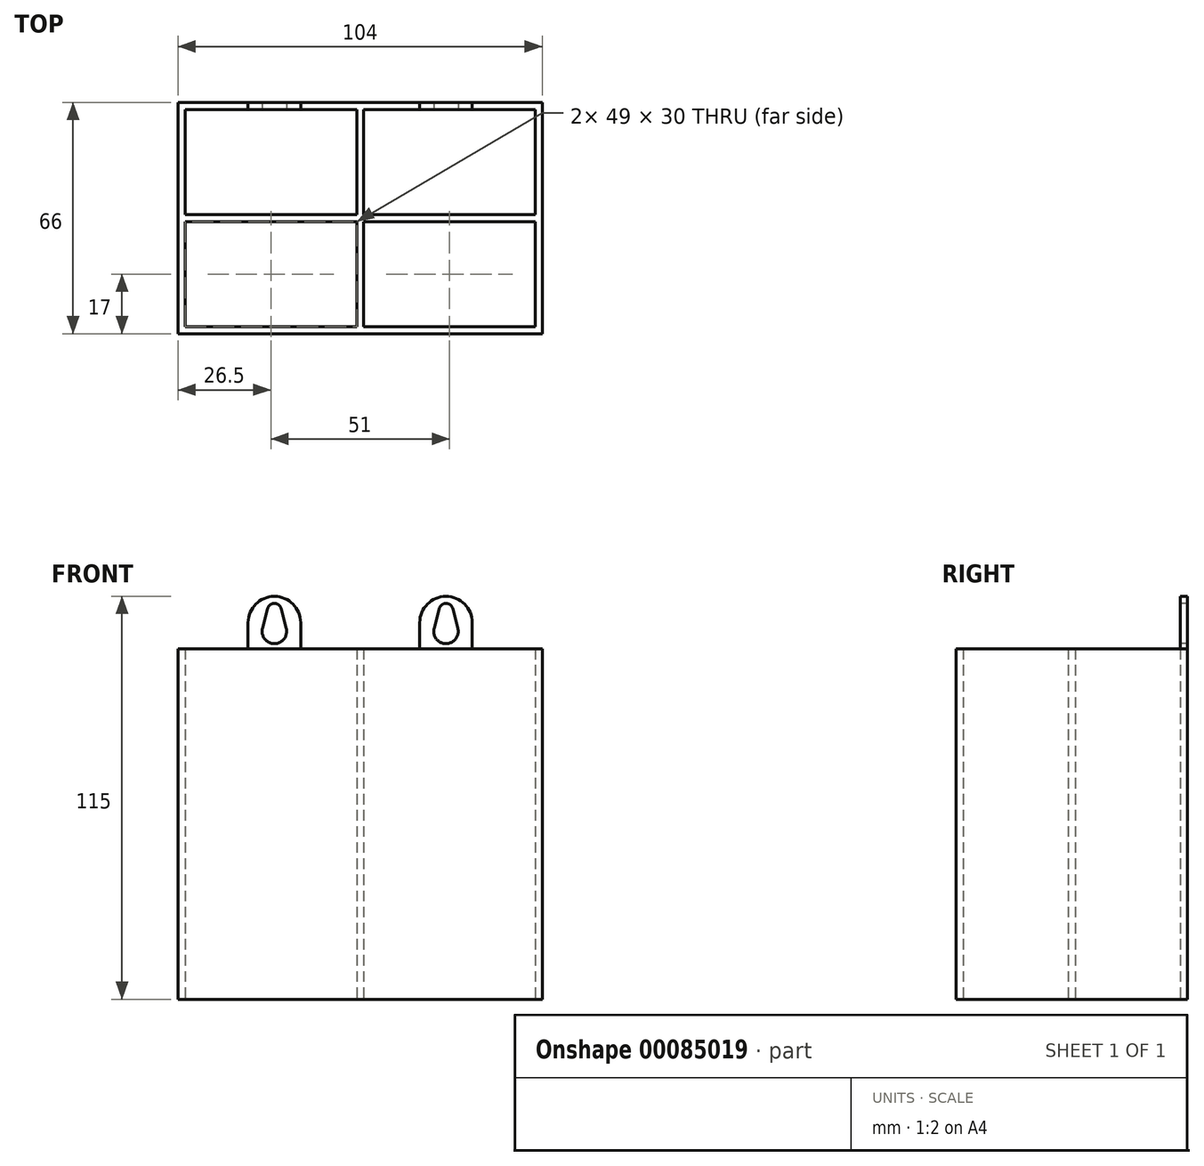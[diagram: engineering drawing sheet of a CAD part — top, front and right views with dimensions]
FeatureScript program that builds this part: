
annotation { "Feature Type Name" : "Feature", "Feature Type Description" : "" }
export const myFeature = defineFeature(function(context is Context, id is Id, definition is map)
    precondition{}
    {
        {
            var Q0;
            Q0=qCreatedBy(makeId("Top.planeOp"),FACE);
            var sketch = newSketch(context, id + "F0", { "sketchPlane" : qUnion([Q0])});
            skLineSegment(sketch, "E0", {"start": v(0, 0) * mm, "end": v(104, 0) * mm});
            skLineSegment(sketch, "E1", {"start": v(0, 0) * mm, "end": v(0, -34) * mm});
            skLineSegment(sketch, "E2", {"start": v(104, 0) * mm, "end": v(104, -34) * mm});
            skLineSegment(sketch, "E3", {"start": v(0, -34) * mm, "end": v(0, -66) * mm});
            skLineSegment(sketch, "E4", {"start": v(0, -66) * mm, "end": v(104, -66) * mm});
            skLineSegment(sketch, "E5", {"start": v(104, -66) * mm, "end": v(104, -34) * mm});
            skSolve(sketch);
        }
        {
            var Q0;
            Q0=qSketchRegion(id+"F0",true);
            extrude(context, id + "F1", {"entities" : qUnion([Q0]), "depth" : 2 * mm});
        }
        {
            var Q0;
            Q0=makeQuery(id+"F1.opExtrude","CAP_FACE",FACE,{"disambiguationData":[OSD([sQuery(id+"F0.wireOp",EDGE,"E0"),sQuery(id+"F0.wireOp",EDGE,"E1"),sQuery(id+"F0.wireOp",EDGE,"E2"),sQuery(id+"F0.wireOp",EDGE,"X1rNKPjP-HQC1-Qpvj-1jiI-HLgqTOV81LFl")])],"isStart":false});
            var sketch = newSketch(context, id + "F2", { "sketchPlane" : qUnion([Q0])});
            skLineSegment(sketch, "E6.bottom", {"start": v(0, 0) * mm, "end": v(104, 0) * mm});
            skLineSegment(sketch, "E6.top", {"start": v(0, -66) * mm, "end": v(104, -66) * mm});
            skLineSegment(sketch, "E6.left", {"start": v(0, 0) * mm, "end": v(0, -66) * mm});
            skLineSegment(sketch, "E6.right", {"start": v(104, 0) * mm, "end": v(104, -66) * mm});
            skLineSegment(sketch, "E7.0", {"start": v(2, -2) * mm, "end": v(51, -2) * mm});
            skLineSegment(sketch, "E7.1", {"start": v(2, -2) * mm, "end": v(2, -32) * mm});
            skLineSegment(sketch, "E7.2", {"start": v(2, -64) * mm, "end": v(51, -64) * mm});
            skLineSegment(sketch, "E7.3", {"start": v(102, -2) * mm, "end": v(102, -32) * mm});
            skLineSegment(sketch, "E8", {"start": v(0, -33) * mm, "end": v(104, -33) * mm, "construction": true});
            skLineSegment(sketch, "E9", {"start": v(52, 0) * mm, "end": v(52, -66) * mm, "construction": true});
            skLineSegment(sketch, "E10", {"start": v(2, -32) * mm, "end": v(51, -32) * mm});
            skLineSegment(sketch, "E11", {"start": v(2, -34) * mm, "end": v(51, -34) * mm});
            skLineSegment(sketch, "E12", {"start": v(51, -2) * mm, "end": v(51, -32) * mm});
            skLineSegment(sketch, "E13", {"start": v(53, -2) * mm, "end": v(53, -32) * mm});
            skLineSegment(sketch, "E14.trimOffspring", {"start": v(2, -34) * mm, "end": v(2, -64) * mm});
            skLineSegment(sketch, "E15.trimOffspring", {"start": v(51, -34) * mm, "end": v(51, -64) * mm});
            skLineSegment(sketch, "E16.trimOffspring", {"start": v(53, -34) * mm, "end": v(102, -34) * mm});
            skLineSegment(sketch, "E17.trimOffspring", {"start": v(53, -32) * mm, "end": v(102, -32) * mm});
            skLineSegment(sketch, "E18.trimOffspring", {"start": v(53, -34) * mm, "end": v(53, -64) * mm});
            skLineSegment(sketch, "E19.trimOffspring", {"start": v(53, -2) * mm, "end": v(102, -2) * mm});
            skLineSegment(sketch, "E20.trimOffspring", {"start": v(102, -34) * mm, "end": v(102, -64) * mm});
            skLineSegment(sketch, "E21.trimOffspring", {"start": v(53, -64) * mm, "end": v(102, -64) * mm});
            skSolve(sketch);
        }
        {
            var Q0;
            Q0=qSketchRegion(id+"F2",true);
            extrude(context, id + "F3", {"entities" : qUnion([Q0]), "operationType" : NewBodyOperationType.ADD, "depth" : 100 * mm});
        }
        {
            var Q0;
            Q0=makeQuery(id+"F3.opExtrude","CAP_FACE",FACE,{"disambiguationData":[OSD([sQuery(id+"F2.wireOp",EDGE,"E6.bottom"),sQuery(id+"F2.wireOp",EDGE,"E6.top"),sQuery(id+"F2.wireOp",EDGE,"E6.left"),sQuery(id+"F2.wireOp",EDGE,"E6.right"),sQuery(id+"F2.wireOp",EDGE,"E7.0"),sQuery(id+"F2.wireOp",EDGE,"E7.1"),sQuery(id+"F2.wireOp",EDGE,"E7.2"),sQuery(id+"F2.wireOp",EDGE,"E7.3"),sQuery(id+"F2.wireOp",EDGE,"E10"),sQuery(id+"F2.wireOp",EDGE,"E11"),sQuery(id+"F2.wireOp",EDGE,"E12"),sQuery(id+"F2.wireOp",EDGE,"E13"),sQuery(id+"F2.wireOp",EDGE,"E14.trimOffspring"),sQuery(id+"F2.wireOp",EDGE,"E15.trimOffspring"),sQuery(id+"F2.wireOp",EDGE,"E16.trimOffspring"),sQuery(id+"F2.wireOp",EDGE,"E17.trimOffspring"),sQuery(id+"F2.wireOp",EDGE,"E18.trimOffspring"),sQuery(id+"F2.wireOp",EDGE,"E19.trimOffspring"),sQuery(id+"F2.wireOp",EDGE,"E20.trimOffspring"),sQuery(id+"F2.wireOp",EDGE,"E21.trimOffspring")])],"isStart":false});
            var sketch = newSketch(context, id + "F4", { "sketchPlane" : qUnion([Q0])});
            skLineSegment(sketch, "E22.bottom", {"start": v(20, 0) * mm, "end": v(35, 0) * mm});
            skLineSegment(sketch, "E22.top", {"start": v(20, -2) * mm, "end": v(35, -2) * mm});
            skLineSegment(sketch, "E22.left", {"start": v(20, 0) * mm, "end": v(20, -2) * mm});
            skLineSegment(sketch, "E22.right", {"start": v(35, 0) * mm, "end": v(35, -2) * mm});
            skLineSegment(sketch, "E23.bottom", {"start": v(69, 0) * mm, "end": v(84, 0) * mm});
            skLineSegment(sketch, "E23.top", {"start": v(69, -2) * mm, "end": v(84, -2) * mm});
            skLineSegment(sketch, "E23.left", {"start": v(69, 0) * mm, "end": v(69, -2) * mm});
            skLineSegment(sketch, "E23.right", {"start": v(84, 0) * mm, "end": v(84, -2) * mm});
            skSolve(sketch);
        }
        {
            var Q0;
            Q0 = qSketchRegion(id + "F4", true);
            extrude(context, id + "F5", {"entities" : qUnion([Q0]), "operationType" : NewBodyOperationType.ADD, "depth" : 15 * mm});
        }
        {
            var Q0;
            Q0=makeQuery(id+"F5.boolean.opBoolean","MERGE",FACE,{"derivedFrom":[makeQuery(id+"F3.opExtrude","SWEPT_FACE",FACE,{"disambiguationData":[OSD([sQuery(id+"F2.wireOp",EDGE,"E7.0")])]}),makeQuery(id+"F5.opExtrude","SWEPT_FACE",FACE,{"disambiguationData":[OSD([sQuery(id+"F4.wireOp",EDGE,"E22.top")])]})]});
            var sketch = newSketch(context, id + "F6", { "sketchPlane" : qUnion([Q0])});
            skLineSegment(sketch, "E24", {"start": v(27.5, 117) * mm, "end": v(27.5, 102) * mm, "construction": true});
            skLineSegment(sketch, "E25.0", {"start": v(69, 117) * mm, "end": v(84, 117) * mm, "construction": true});
            skPoint(sketch, "E26", {"position": v(76.5, 117) * mm});
            skLineSegment(sketch, "E27", {"start": v(76.5, 117) * mm, "end": v(76.5, 102) * mm, "construction": true});
            skArc(sketch, "E28", {"start": v(78.44, 113.5) * mm, "mid": v(76.5, 115) * mm, "end": v(74.56, 113.5) * mm});
            skArc(sketch, "E29", {"start": v(73.11, 107.88) * mm, "mid": v(76.5, 103.5) * mm, "end": v(79.89, 107.88) * mm});
            skArc(sketch, "E30", {"start": v(29.44, 113.5) * mm, "mid": v(27.5, 115) * mm, "end": v(25.56, 113.5) * mm});
            skArc(sketch, "E31", {"start": v(24.11, 107.88) * mm, "mid": v(27.5, 103.5) * mm, "end": v(30.89, 107.88) * mm});
            skLineSegment(sketch, "E32", {"start": v(25.56, 113.5) * mm, "end": v(24.11, 107.88) * mm});
            skLineSegment(sketch, "E33", {"start": v(29.44, 113.5) * mm, "end": v(30.89, 107.88) * mm});
            skLineSegment(sketch, "E34", {"start": v(74.56, 113.5) * mm, "end": v(73.11, 107.88) * mm});
            skLineSegment(sketch, "E35", {"start": v(78.44, 113.5) * mm, "end": v(79.89, 107.88) * mm});
            skSolve(sketch);
        }
        {
            var Q0;
            Q0 = qSketchRegion(id + "F6", true);
            var Q1;
            Q1=makeQuery(id+"F5.boolean.opBoolean","MERGE",FACE,{"derivedFrom":[makeQuery(id+"F3.boolean.opBoolean","MERGE",FACE,{"derivedFrom":[makeQuery(id+"F1.opExtrude","SWEPT_FACE",FACE,{"disambiguationData":[OSD([sQuery(id+"F0.wireOp",EDGE,"E0")])]}),makeQuery(id+"F3.opExtrude","SWEPT_FACE",FACE,{"disambiguationData":[OSD([sQuery(id+"F2.wireOp",EDGE,"E6.bottom")])]})]}),makeQuery(id+"F5.opExtrude","SWEPT_FACE",FACE,{"disambiguationData":[OSD([sQuery(id+"F4.wireOp",EDGE,"E22.bottom")])]}),makeQuery(id+"F5.opExtrude","SWEPT_FACE",FACE,{"disambiguationData":[OSD([sQuery(id+"F4.wireOp",EDGE,"E23.bottom")])]})]});
            extrude(context, id + "F7", {"entities" : qUnion([Q0]), "operationType" : NewBodyOperationType.REMOVE, "endBound" : BoundingType.UP_TO_SURFACE, "oppositeDirection" : true, "endBoundEntityFace" : qUnion([Q1]), "depth" : 25 * mm});
        }
        {
            var Q0;
            Q0=makeQuery(id+"F5.opExtrude","CAP_EDGE",EDGE,{"disambiguationData":[OSD([sQuery(id+"F4.wireOp",EDGE,"E23.right")])],"isStart":true});
            var Q1;
            Q1=makeQuery(id+"F5.opExtrude","CAP_EDGE",EDGE,{"disambiguationData":[OSD([sQuery(id+"F4.wireOp",EDGE,"E23.right")])],"isStart":false});
            var Q2;
            Q2=makeQuery(id+"F5.opExtrude","CAP_EDGE",EDGE,{"disambiguationData":[OSD([sQuery(id+"F4.wireOp",EDGE,"E23.left")])],"isStart":false});
            var Q3;
            Q3=makeQuery(id+"F5.opExtrude","CAP_EDGE",EDGE,{"disambiguationData":[OSD([sQuery(id+"F4.wireOp",EDGE,"E23.left")])],"isStart":true});
            var Q4;
            Q4=makeQuery(id+"F5.opExtrude","CAP_EDGE",EDGE,{"disambiguationData":[OSD([sQuery(id+"F4.wireOp",EDGE,"E22.right")])],"isStart":true});
            var Q5;
            Q5=makeQuery(id+"F5.opExtrude","CAP_EDGE",EDGE,{"disambiguationData":[OSD([sQuery(id+"F4.wireOp",EDGE,"E22.right")])],"isStart":false});
            var Q6;
            Q6=makeQuery(id+"F5.opExtrude","CAP_EDGE",EDGE,{"disambiguationData":[OSD([sQuery(id+"F4.wireOp",EDGE,"E22.left")])],"isStart":false});
            var Q7;
            Q7=makeQuery(id+"F5.opExtrude","CAP_EDGE",EDGE,{"disambiguationData":[OSD([sQuery(id+"F4.wireOp",EDGE,"E22.left")])],"isStart":true});
            fillet(context, id + "F8", {"entities" : qUnion([Q0, Q1, Q2, Q3, Q4, Q5, Q6, Q7]), "radius" : 7.5 * mm, "tangentPropagation" : true, "allowEdgeOverflow" : false});
        }
        {
            var Q0;
            Q0=makeQuery(id+"F1.opExtrude","CAP_FACE",FACE,{"disambiguationData":[OSD([sQuery(id+"F0.wireOp",EDGE,"E0"),sQuery(id+"F0.wireOp",EDGE,"E1"),sQuery(id+"F0.wireOp",EDGE,"E2"),sQuery(id+"F0.wireOp",EDGE,"E3"),sQuery(id+"F0.wireOp",EDGE,"E4"),sQuery(id+"F0.wireOp",EDGE,"E5")])],"isStart":true});
            var sketch = newSketch(context, id + "F9", { "sketchPlane" : qUnion([Q0])});
            skLineSegment(sketch, "E36.bottom", {"start": v(0, 0) * mm, "end": v(104, 0) * mm});
            skLineSegment(sketch, "E36.top", {"start": v(0, 66) * mm, "end": v(104, 66) * mm});
            skLineSegment(sketch, "E36.left", {"start": v(0, 0) * mm, "end": v(0, 66) * mm});
            skLineSegment(sketch, "E36.right", {"start": v(104, 0) * mm, "end": v(104, 66) * mm});
            skSolve(sketch);
        }
        {
            var Q0;
            Q0 = qSketchRegion(id + "F9", true);
            extrude(context, id + "F10", {"entities" : qUnion([Q0]), "operationType" : NewBodyOperationType.REMOVE, "oppositeDirection" : true, "depth" : 2 * mm});
        }
    });
